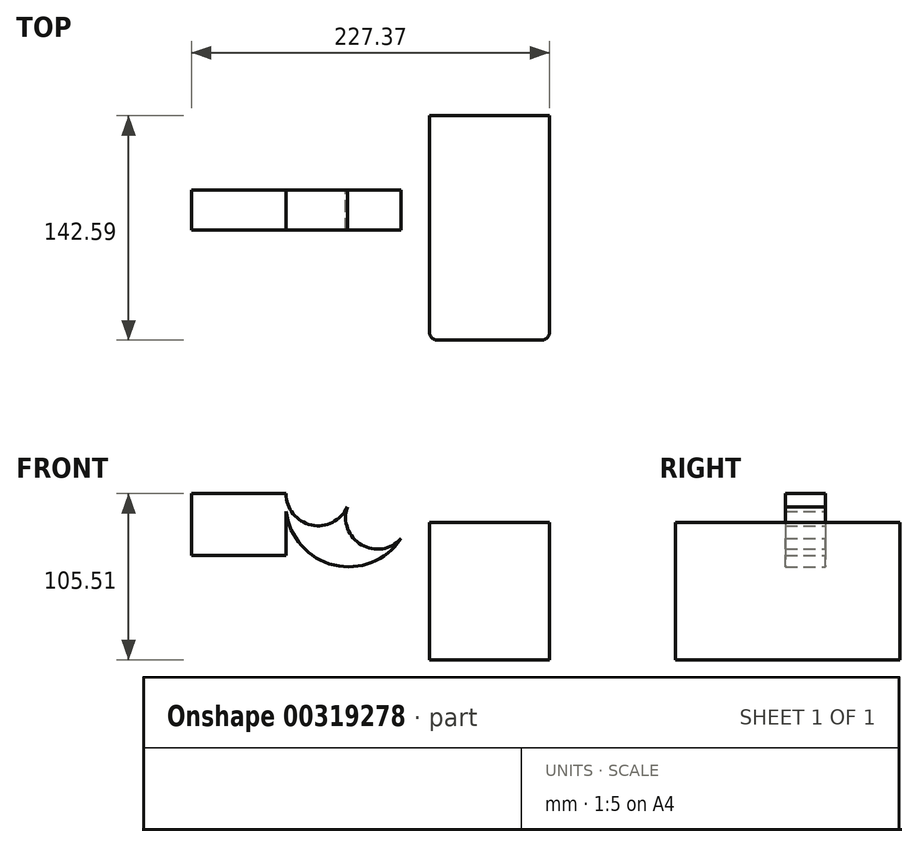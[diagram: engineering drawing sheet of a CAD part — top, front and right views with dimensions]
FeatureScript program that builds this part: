
annotation { "Feature Type Name" : "Feature", "Feature Type Description" : "" }
export const myFeature = defineFeature(function(context is Context, id is Id, definition is map)
    precondition{}
    {
        {
            var Q0;
            Q0=qCreatedBy(makeId("Front.planeOp"),FACE);
            var sketch = newSketch(context, id + "F0", { "sketchPlane" : qUnion([Q0])});
            skLineSegment(sketch, "E0.bottom", {"start": v(-91.05, 43.78) * mm, "end": v(-151.17, 43.78) * mm});
            skLineSegment(sketch, "E0.top", {"start": v(-91.05, 4.57) * mm, "end": v(-151.17, 4.57) * mm});
            skLineSegment(sketch, "E0.left", {"start": v(-91.05, 43.78) * mm, "end": v(-91.05, 4.57) * mm});
            skLineSegment(sketch, "E0.right", {"start": v(-151.17, 43.78) * mm, "end": v(-151.17, 4.57) * mm});
            skCircle(sketch, "E1", {"center": v(-51.4, 37.25) * mm, "radius": 39.9 * mm});
            skArc(sketch, "E2", {"start": v(-91.05, 43.78) * mm, "mid": v(-74, 23.7) * mm, "end": v(-51.4, 37.25) * mm});
            skArc(sketch, "E3", {"start": v(-51.4, 37.25) * mm, "mid": v(-38.81, 9.4) * mm, "end": v(-13.13, 25.96) * mm});
            skSolve(sketch);
        }
        {
            var Q0;
            {var subQ0=sQuery(id+"F0.wireOp",EDGE,"E3");var subQ1=sQuery(id+"F0.wireOp",EDGE,"E1");var subQ2=makeQuery(id+"F0.imprint","INTERSECT",VERTEX,{"disambiguationData":[OD(0.0)],"derivedFrom":[subQ1,subQ0]});Q0=makeQuery(id+"F0.imprint","IMPRINT",FACE,{"disambiguationData":[TD([[makeQuery(id+"F0.imprint","IMPRINT",EDGE,{"disambiguationData":[TD([[subQ2,1.0]])],"derivedFrom":subQ1}),-1.0]])]});}
            var Q1;
            {var subQ4=sQuery(id+"F0.wireOp",EDGE,"E0.bottom");Q1=makeQuery(id+"F0.imprint","IMPRINT",FACE,{"disambiguationData":[TD([[makeQuery(id+"F0.imprint","IMPRINT",EDGE,{"derivedFrom":subQ4}),1.0]])]});}
            var Q2;
            {var subQ0=sQuery(id+"F0.wireOp",EDGE,"E2");var subQ3=sQuery(id+"F0.wireOp",EDGE,"E1");var subQ5=makeQuery(id+"F0.imprint","INTERSECT",VERTEX,{"derivedFrom":[subQ3,subQ0]});Q2=makeQuery(id+"F0.imprint","IMPRINT",FACE,{"disambiguationData":[TD([[makeQuery(id+"F0.imprint","IMPRINT",EDGE,{"disambiguationData":[TD([[subQ5,-1.0]])],"derivedFrom":subQ3}),-1.0]])]});}
            var Q3;
            {var subQ0=sQuery(id+"F0.wireOp",EDGE,"E1");var subQ1=sQuery(id+"F0.wireOp",EDGE,"E0.left");var subQ2=makeQuery(id+"F0.imprint","INTERSECT",VERTEX,{"disambiguationData":[OD(0.0)],"derivedFrom":[subQ1,subQ0]});Q3=makeQuery(id+"F0.imprint","IMPRINT",FACE,{"disambiguationData":[TD([[makeQuery(id+"F0.imprint","IMPRINT",EDGE,{"disambiguationData":[TD([[subQ2,1.0]])],"derivedFrom":subQ1}),-1.0]])]});}
            var Q4;
            {var subQ0=sQuery(id+"F0.wireOp",EDGE,"E3");var subQ4=sQuery(id+"F0.wireOp",EDGE,"E1");var subQ6=makeQuery(id+"F0.imprint","INTERSECT",VERTEX,{"disambiguationData":[OD(0.0)],"derivedFrom":[subQ4,subQ0]});Q4=makeQuery(id+"F0.imprint","IMPRINT",FACE,{"disambiguationData":[TD([[makeQuery(id+"F0.imprint","IMPRINT",EDGE,{"disambiguationData":[TD([[subQ6,1.0]])],"derivedFrom":subQ4}),1.0]])]});}
            extrude(context, id + "F1", {"entities" : qUnion([Q0, Q1, Q2, Q3, Q4]), "depth" : 25.4 * mm});
        }
        {
            var Q0;
            Q0=qCreatedBy(makeId("Right.planeOp"),FACE);
            var sketch = newSketch(context, id + "F2", { "sketchPlane" : qUnion([Q0])});
            skLineSegment(sketch, "E4.bottom", {"start": v(47.25, 25.45) * mm, "end": v(-95.34, 25.45) * mm});
            skLineSegment(sketch, "E4.top", {"start": v(47.25, -61.73) * mm, "end": v(-95.34, -61.73) * mm});
            skLineSegment(sketch, "E4.left", {"start": v(47.25, 25.45) * mm, "end": v(47.25, -61.73) * mm});
            skLineSegment(sketch, "E4.right", {"start": v(-95.34, 25.45) * mm, "end": v(-95.34, -61.73) * mm});
            skSolve(sketch);
        }
        {
            var Q0;
            Q0=makeQuery(id+"F2.imprint","IMPRINT",FACE,{"disambiguationData":[TD([[makeQuery(id+"F2.imprint","IMPRINT",EDGE,{"derivedFrom":sQuery(id+"F2.wireOp",EDGE,"E4.bottom")}),1.0]])]});
            extrude(context, id + "F3", {"entities" : qUnion([Q0]), "depth" : 76.2 * mm});
        }
        {
            var Q0;
            Q0=makeQuery(id+"F3.opExtrude","CAP_EDGE",EDGE,{"disambiguationData":[OSD([sQuery(id+"F2.wireOp",EDGE,"E4.right")])],"isStart":true});
            var Q1;
            Q1=makeQuery(id+"F3.opExtrude","CAP_EDGE",EDGE,{"disambiguationData":[OSD([sQuery(id+"F2.wireOp",EDGE,"E4.right")])],"isStart":false});
            fillet(context, id + "F4", {"entities" : qUnion([Q0, Q1]), "radius" : 5.08 * mm, "tangentPropagation" : true, "allowEdgeOverflow" : false});
        }
    });
